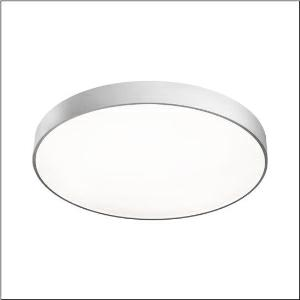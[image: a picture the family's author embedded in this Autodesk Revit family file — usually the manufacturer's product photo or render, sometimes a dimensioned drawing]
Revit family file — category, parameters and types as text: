
# Revit family: round_21_l_51mr38fd0321s
name_source: partatom
category: Lighting Fixtures
units: mm (PartAtom-declared; Revit-internal decimal feet)

## family parameters
Cut with Voids When Loaded = No
Host = Face
Light Source = No
Part Type = Normal
Room Calculation Point = No
Round Connector Dimension = Use Diameter
Shared = No

## types (1)
- Round 21 L (1 x LED, 12490 lm, 98.3 W, 3000K)
    Apparent Load = 98 VA
    CIE Flux Codes = 49 80 96 100 100
    Color Rendering = 80
    Color Temperature = 3000K
    Default Elevation = 1800 mm
    Description = Round 21 L, wall and ceiling luminaire, primary optical cover: cover, of PMMA, opal, light emission: direct distribution, primary light characteristic: symmetric, installation type: suspended mounting, surface-mounted, LED, rated luminous flux: 12.490lm, luminous efficacy: 127lm/W, light colour: 830, colour temperature: 3000K, with terminal, 5-pole, mains connection: 230V, AC, 50/60Hz, rated input power: 98W, housing, of aluminium, coated, silver, diameter: 850mm, height: 62mm, protection rating (complete): IP40, insulation class (complete): insulation class I (protective earthing), certification: CE, impact resistance: IK04, permissible operating ambient temperature: -10..+35°C, packaging unit: 1 piece
    Height = 87 mm
    Lamp = 1 x LED
    Lamp Light Flux = 12490 lm
    Lamp Power = 98.3 W
    Lamp count = 1
    Length = 850 mm
    Luminous efficacy = 127 lm/W
    Manufacturer = Siteco
    ModVariant = No
    Model = 51MR38FD0321S
    Mounting Place = Ceiling
    Mounting Type = Surface mounted
    Number of Poles = 1
    OnlyDefault = Yes
    Power Factor = 1
    Product Name = Round 21 L
    Product group = wall and ceiling luminaire
    ProductGroupID = 301
    Protection Class = Protection class I
    Protection Degree = IP 40
    RLX_Detail_Level = 1
    RLX_Emergency_Light_Flux = 0 lm
    RLX_Emergency_Type = 0
    RLX_Emergency_Type_DB = No
    RlxData = <blob elided: 20205 chars, md5=193a29b0>
    Socket = socket
    Standby Power = 0 W
    System Light Flux = 12490 lm
    System Power = 98 W
    Type Comments = Product without accessories
    Type Image = l_1258324.jpg
    URL = http://relux.com
    VarID = ---
    Voltage = 0 V
    Weight = 0.00 kg
    Width = 0 mm  [stored 0 ft]

note: [stored X ft] marks values corroborated as IEEE doubles in the binary element streams (Revit-internal decimal feet)

## geometry (parser evidence)
native form markers: Blend x4, Sweep x11
no freeform markers — native parametric forms only
